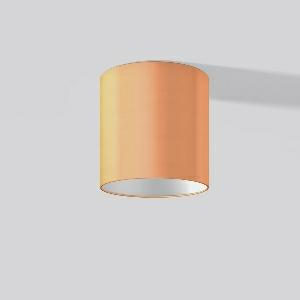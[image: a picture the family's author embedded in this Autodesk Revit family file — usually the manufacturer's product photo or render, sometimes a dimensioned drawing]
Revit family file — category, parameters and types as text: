
# Revit family: toledo_flatliner_901634_002_1_be23
name_source: partatom
category: Lighting Fixtures
units: mm (PartAtom-declared; Revit-internal decimal feet)

## family parameters
Cut with Voids When Loaded = No
Host = Face
Light Source = No
Part Type = Normal
Room Calculation Point = No
Round Connector Dimension = Use Diameter
Shared = No

## types (1)
- 982302.002 (1 x LED Modul 840, 1950 lm, 4000)
    Apparent Load = 22 VA
    CIE Flux Codes = 50 82 97 99 100
    Color Rendering = 80
    Color Temperature = 4000
    Default Elevation = 1800 mm
    Description = Series: TOLEDO FLATLINER
Decorative ceiling luminaire for interior decoration. Base luminaire prepared for the installation of fabric lampshade. Cylinder housing sheet steel, powder-coated. Housing: die cast aluminium and sheet steel, powder-coated. Bezel ring: die-cast aluminium, powder-coated. Lightguide and diffuser made of non-yellowing plastic (PMMA) opal matt. Modular design: With the basic luminaire, a square or cylindrical fabric lampshade must always be ordered separately. Fabric lampshades can be fitted to the basic luminaire without tools. Order satin finish diffuser as separate accessory. 
Colour: white
Diameter: 330 mm
Height: 70 mm
Lamp: LED
Socket: without socket
Colour temperature: 4000K
Colour rendering index (CRI): 80
System power: 22 W
Rated luminous flux: 1950 lm
Luminous efficiency: 89 lm/W
Control gear: Regulated power supply
Protection class: II
Type of protection: IP 40
    Height = 70 mm
    Lamp = 1 x LED Modul 840
    Lamp Light Flux = 1950 lm
    Lamp count = 1
    Length = 330 mm
    Lifetime = 50000 h
    Luminous efficacy = 89 lm/W
    Manufacturer = RZB
    ModVariant = No
    Model = 901634.002.1
    Mounting Place = Ceiling
    Mounting Type = Surface mounted
    Number of Poles = 1
    OnlyDefault = Yes
    Power Factor = 1
    Product Name = TOLEDO FLATLINER
    Product group = Surface mounted ceiling Fabric lampshade luminaires
    ProductGroupID = 313
    Protection Class = Protection class II
    Protection Degree = IP 40
    RLX_Detail_Level = 1
    RLX_Emergency_Light_Flux = 0 lm
    RLX_Emergency_Type = 0
    RLX_Emergency_Type_DB = No
    RlxData = <blob elided: 62705 chars, md5=4d1e882d>
    Socket = socket
    Standby Power = 0 W
    System Light Flux = 1950 lm
    System Power = 22 W
    Type Image = toledo_flatliner_anbau_rund_orange_odeckel.jpg
    URL = http://relux.com
    VarID = 982302_002_891e
    Voltage = 230 V
    Voltage Range = 220-240 V
    Weight = 0.00 kg
    Width = 0 mm  [stored 0 ft]

note: [stored X ft] marks values corroborated as IEEE doubles in the binary element streams (Revit-internal decimal feet)

## geometry (parser evidence)
native form markers: Blend x4, Sweep x9
no freeform markers — native parametric forms only
